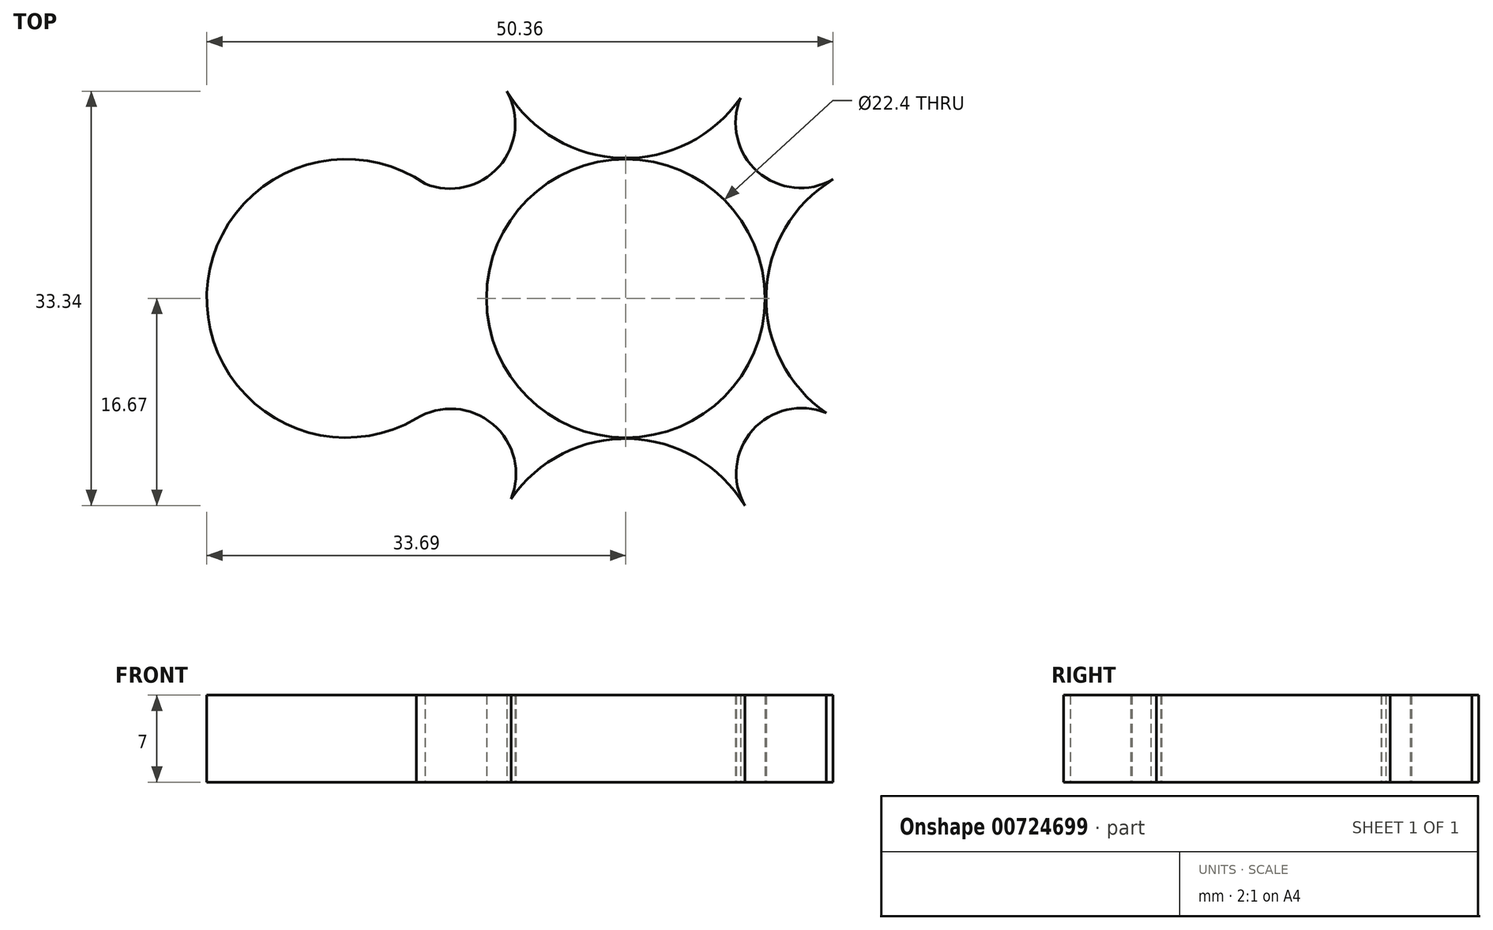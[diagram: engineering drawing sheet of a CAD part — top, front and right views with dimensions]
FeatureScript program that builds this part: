
annotation { "Feature Type Name" : "Feature", "Feature Type Description" : "" }
export const myFeature = defineFeature(function(context is Context, id is Id, definition is map)
    precondition{}
    {
        {
            var Q0;
            Q0=qCreatedBy(makeId("Top.planeOp"),FACE);
            var sketch = newSketch(context, id + "F0", { "sketchPlane" : qUnion([Q0])});
            skCircle(sketch, "E0", {"center": v(0, 0) * mm, "radius": 11.2 * mm});
            skCircle(sketch, "E1", {"center": v(0, 22.49) * mm, "radius": 11.2 * mm});
            skCircle(sketch, "E2.1.0", {"center": v(-22.49, 0) * mm, "radius": 11.2 * mm});
            skCircle(sketch, "E2.2.0", {"center": v(0, -22.49) * mm, "radius": 11.2 * mm});
            skCircle(sketch, "E2.3.0", {"center": v(22.49, 0) * mm, "radius": 11.2 * mm});
            skArc(sketch, "E3", {"start": v(9.22, 16.13) * mm, "mid": v(10.68, 10.13) * mm, "end": v(16.84, 9.67) * mm});
            skArc(sketch, "E4.1.0", {"start": v(-16.13, 9.22) * mm, "mid": v(-10.13, 10.68) * mm, "end": v(-9.67, 16.84) * mm});
            skArc(sketch, "E4.2.0", {"start": v(-9.22, -16.13) * mm, "mid": v(-10.68, -10.13) * mm, "end": v(-16.84, -9.67) * mm});
            skArc(sketch, "E4.3.0", {"start": v(16.13, -9.22) * mm, "mid": v(10.13, -10.68) * mm, "end": v(9.67, -16.84) * mm});
            skSolve(sketch);
        }
        {
            var Q0;
            Q0=makeQuery(id+"F0.imprint","IMPRINT",FACE,{"disambiguationData":[TD([[makeQuery(id+"F0.imprint","IMPRINT",EDGE,{"derivedFrom":sQuery(id+"F0.wireOp",EDGE,"E0")}),-1.0]])]});
            var Q1;
            {var subQ0=sQuery(id+"F0.wireOp",EDGE,"E2.1.0");var subQ1=makeQuery(id+"F0.imprint","INTERSECT",VERTEX,{"derivedFrom":[subQ0,sQuery(id+"F0.wireOp",EDGE,"E4.1.0")]});Q1=makeQuery(id+"F0.imprint","IMPRINT",FACE,{"disambiguationData":[TD([[makeQuery(id+"F0.imprint","IMPRINT",EDGE,{"disambiguationData":[TD([[subQ1,1.0]])],"derivedFrom":subQ0}),1.0]])]});}
            extrude(context, id + "F1", {"entities" : qUnion([Q0, Q1]), "depth" : 7 * mm, "offsetDistance" : 25 * mm});
        }
    });
